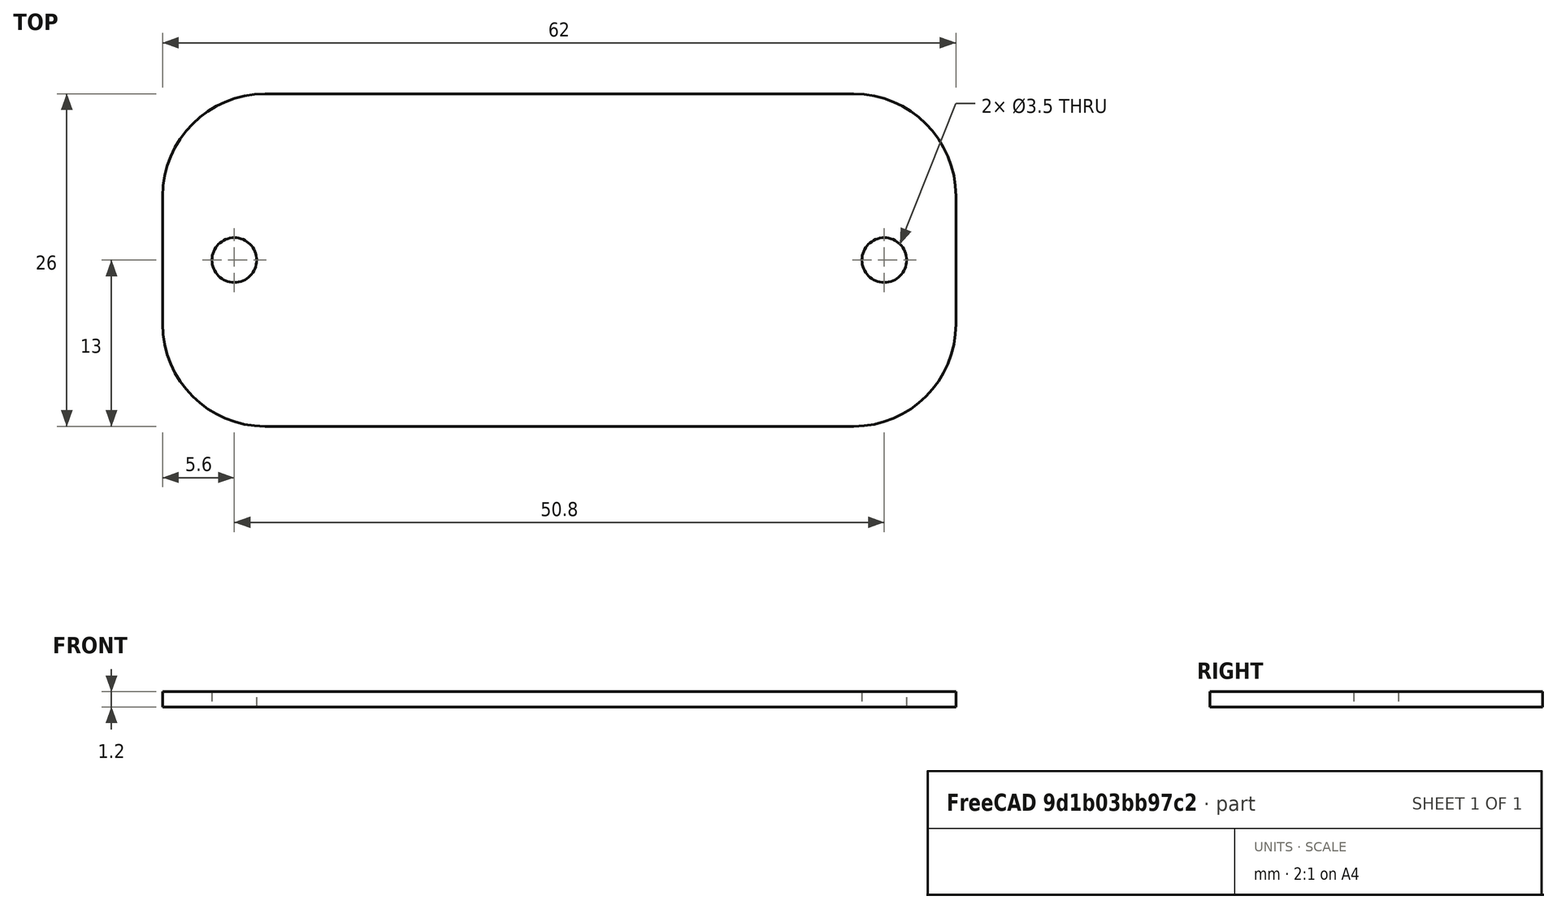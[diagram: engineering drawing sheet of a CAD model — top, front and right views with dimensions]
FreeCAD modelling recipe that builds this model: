
FCSTD DOCUMENT  (FreeCAD 0.16R6712 (Git))
Label: Nameplate
License: All rights reserved
LicenseURL: http://en.wikipedia.org/wiki/All_rights_reserved
objects: PartDesign::Body×1, Sketcher::SketchObject×1, PartDesign::Pad×1
note: 4 computed .brp shape members not serialized (recipe doc carries the construction recipe); baked Part::Feature solids carry a one-line shape summary decoded from their .brp

FEATURE [PartDesign::Body] Body
FEATURE [Sketcher::SketchObject] Sketch  label="nose"
  expr: Constraints[13] = 3.5mm / 2
  expr: Constraints[16] = 3.5mm / 2
  sketch-geometry (10):
    g0: LineSegment StartX=-23 StartY=22 StartZ=0 EndX=23 EndY=22 EndZ=0
    g1: LineSegment StartX=31 StartY=14 StartZ=0 EndX=31 EndY=8 EndZ=0
    g2: LineSegment StartX=23 StartY=0 StartZ=0 EndX=-23 EndY=0 EndZ=0
    g3: LineSegment StartX=-31 StartY=8 StartZ=0 EndX=-31 EndY=14 EndZ=0
    g4: ArcOfCircle CenterX=-23 CenterY=8 CenterZ=0 NormalX=0 NormalY=0 NormalZ=1 Radius=8 StartAngle=3.14159 EndAngle=4.71239
    g5: ArcOfCircle CenterX=23 CenterY=8 CenterZ=0 NormalX=0 NormalY=0 NormalZ=1 Radius=8 StartAngle=4.71239 EndAngle=6.28319
    g6: Circle CenterX=-25.4 CenterY=11 CenterZ=0 NormalX=0 NormalY=0 NormalZ=1 Radius=1.75
    g7: Circle CenterX=25.4 CenterY=11 CenterZ=0 NormalX=0 NormalY=0 NormalZ=1 Radius=1.75
    g8: ArcOfCircle CenterX=-23 CenterY=14 CenterZ=0 NormalX=0 NormalY=0 NormalZ=1 Radius=8 StartAngle=1.5708 EndAngle=3.14159
    g9: ArcOfCircle CenterX=23 CenterY=14 CenterZ=0 NormalX=0 NormalY=0 NormalZ=1 Radius=8 StartAngle=0 EndAngle=1.5708
  constraints (26):
    c: Horizontal(g0)
    c: Horizontal(g2)
    c: Vertical(g1)
    c: Vertical(g3)
    c: Tangent(g2,g4) = 1.5708
    c: Tangent(g3,g4) = 1.5708
    c: DistanceX(g3,g4) = 8
    c: DistanceY(g2,g-1) = 0
    c: Tangent(g1,g5) = 1.5708
    c: Tangent(g2,g5) = 1.5708
    c: DistanceY(g2,g5) = 8
    c: DistanceY(g2,g6) = 11
    c: DistanceX(g6,g-1) = 25.4
    c: Radius(g6) = 1.75
    c: DistanceY(g2,g7) = 11
    c: DistanceX(g-1,g7) = 25.4
    c: Radius(g7) = 1.75
    c: Tangent(g0,g8) = 1.5708
    c: Tangent(g3,g8) = 1.5708
    c: Tangent(g0,g9) = 1.5708
    c: Tangent(g1,g9) = 1.5708
    c: DistanceX(g3,g8) = 8
    c: DistanceY(g9,g0) = 8
    c: DistanceX(g3,g1) = 62
    c: DistanceY(g6,g0) = 11
    c: Symmetric(g3,g1,g-2)
FEATURE [PartDesign::Pad] Pad
  Length = 1.6
  Length2 = 100
  Sketch = -> Sketch
  Type = 0
